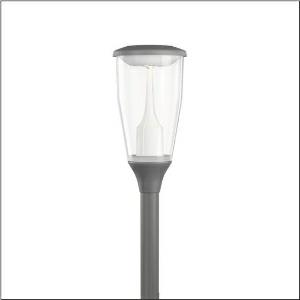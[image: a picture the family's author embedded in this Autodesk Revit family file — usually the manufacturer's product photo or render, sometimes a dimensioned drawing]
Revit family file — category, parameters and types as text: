
# Revit family: dl_11_iq___st1_2a_5xa5565kf14h000022_1156
name_source: partatom
category: Lighting Fixtures
units: mm (PartAtom-declared; Revit-internal decimal feet)

## family parameters
Cut with Voids When Loaded = No
Host = Face
Light Source = No
Part Type = Normal
Room Calculation Point = No
Round Connector Dimension = Use Diameter
Shared = No

## types (1)
- --- (1 x LED, 1560 lm, 10 W, 4000K)
    Apparent Load = 10 VA
    CIE Flux Codes = 24 63 94 96 100
    Color Rendering = 70
    Color Temperature = 4000K
    Default Elevation = 1800 mm
    Description = DL 11 iQ, mast luminaire, Module 540 iQ-SR, primary light control with 3 zone facetted reflector, of plastic, silver coated, highly specular, structured, primary optical cover: cover, of PMMA, transparent, light distribution: ST1.2a, light emission: direct distribution, primary light characteristic: asymmetric, installation type: post-top, LED, High Power LED, rated luminous flux: 1.560lm, luminous efficacy: 149lm/W, light colour: 740, colour temperature: 4000K, control gear: iQ Street-Remote, control: Street-Remote, Auto-Match, Temp-Guard, Lumen-Switch, Night-Set, Smart-Wire, Light-Fading, Desk-Remote (wireless, voltage-free reading and setting of iQ features in the workshop via application-optimized NFC function/RFID function), optimised constant luminous flux control (CLO 2.0), mains connection: 220..240V, AC, 50/60Hz, connection cable pre-assembled, cable length: 5,5m, start of lifetime: 10W, end of service life: 10W, reduction: 5W, luminaire housing, upper part, of diecast aluminium, coated, SITECO metallic grey (DB 702S), spigot size: 60mm (post-top), mounting height: 3..5m, post-top mast mounting element, of diecast aluminium, coated, SITECO metallic grey (DB 702S), Module 540 iQ-SR, traffic white (RAL 9016), equipment: standard, protection rating (complete): IP66, insulation class (complete): insulation class II (safety insulation), certification: CE, ENEC, ENEC+, VDE, impact resistance: IK07, packaging unit: 1 piece

Light Distribution: ST1.2a
    Height = 665 mm
    Lamp = 1 x LED
    Lamp Light Flux = 1560 lm
    Lamp Power = 10 W
    Lamp count = 1
    Length = 334 mm
    Luminous efficacy = 156 lm/W
    Manufacturer = Siteco
    ModVariant = No
    Model = 5XA5565KF14H000022
    Number of Poles = 1
    OnlyDefault = Yes
    Power Factor = 1
    Product Name = DL 11 iQ | ST1.2a
    Product group = mast luminaire | pylon top
    ProductGroupID = 6100
    Protection Class = Protection class II
    Protection Degree = IP 66
    RLX_Detail_Level = 1
    RLX_Emergency_Light_Flux = 0 lm
    RLX_Emergency_Type = 0
    RLX_Emergency_Type_DB = No
    RlxData = <blob elided: 156641 chars, md5=4356d12e>
    Socket = socket
    Standby Power = 0 W
    System Light Flux = 1560 lm
    System Power = 10 W
    Type Comments = factory setting: luminous flux: 100 % | dim-lin: 254 | 401 mA
    Type Image = l_1258354.jpg
    URL = http://relux.com
    VarID = @adj_099065
    Voltage = 0 V
    Weight = 0.00 kg
    Width = 0 mm  [stored 0 ft]

note: [stored X ft] marks values corroborated as IEEE doubles in the binary element streams (Revit-internal decimal feet)

## geometry (parser evidence)
native form markers: Blend x4, Sweep x11
no freeform markers — native parametric forms only
